# Revit family: CVRB-CM
name_source: partatom
category: Lighting Fixtures
revit_build: Autodesk Revit 2013 (Build: 20130531_2115(x64)
units: mm (PartAtom-declared; Revit-internal decimal feet)

## types (4) — shared parameters
Assembly Code = D5020200
Color Filter = 16777215
Default Elevation = 48"
Description = An attractive curvature shape with white-painted baffles that span the radius of the luminaire housing is delivered with the Curv Radial Baffle
Dimming Lamp Color Temperature Shift = <None>
Emit Shape Visible in Rendering = No
Emit from Rectangle Length = 46"
Emit from Rectangle Width = 7"
Glass = Hubbell - White Glass
Housing Material = Hubbell - White
Lamp = T5, T5HO, T8
Load Classification = Lighting
Manufacturer = Alera Lighting
Model = CVRB
Photometric Notes = More IES files download on Photometric Web Link
Photometric Web Link = https://www.hubbell.com
Power Factor = 1
Product Documentation Link = https://hubbellcdn.com
Product Page URL = https://www.hubbell.com
Row Length = 48"
Suspension Height = 48"
Tilt Angle = -90.00°
URL = https://www.hubbell.com
Voltage = 120 V

## per-type parameters (varying)
| type | Apparent Load | Lamp Type | Photometric Web File | Watts |
| CVRB-1T8-EPU | 29 VA | One T8 Lamp | CVRB-1T8-EPU.ies | 29 W |
| CVRB-2T5HO-EPU | 125 VA | Two T5HO Lamps | CVRB-2T5HO-EPU.ies | 125 W |
| CVRB-3T8-EPU | 84 VA | Three T8 Lamps | CVRB-3T8-EPU.ies | 84 W |
| CVRB-4-2T5-WCB-EPU | 63 VA | Two T5 Lamps | CVRB-4-2T5-WCB-EPU.ies | 63 W |

## geometry (parser evidence)
native form markers: Blend x4, Sweep x5
no freeform markers — native parametric forms only
